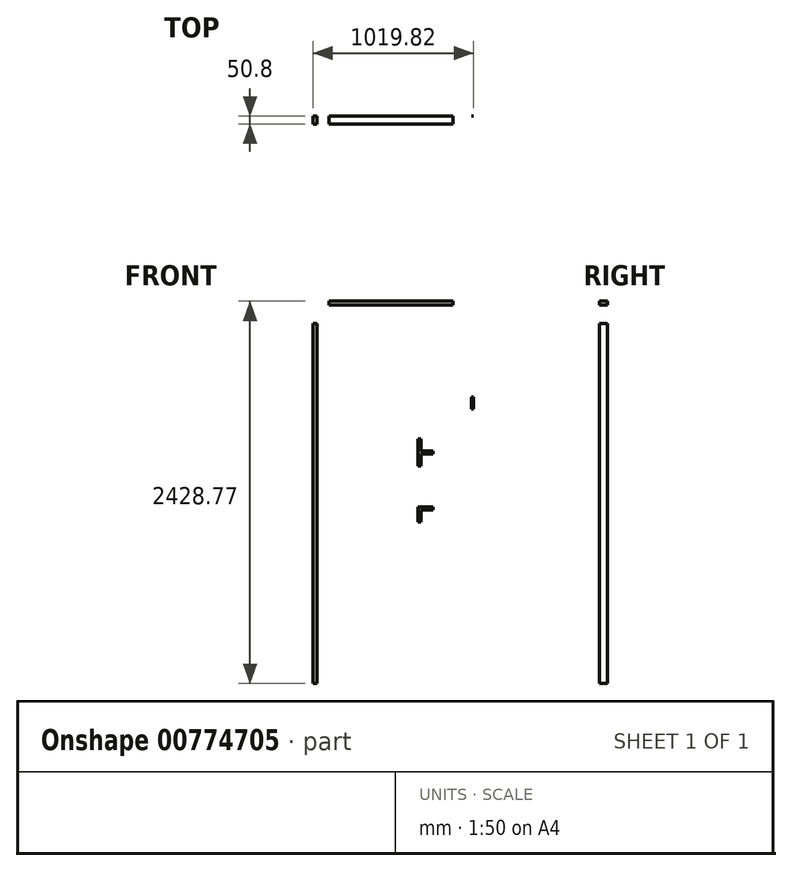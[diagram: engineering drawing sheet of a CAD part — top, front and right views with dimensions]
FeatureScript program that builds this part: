
annotation { "Feature Type Name" : "Feature", "Feature Type Description" : "" }
export const myFeature = defineFeature(function(context is Context, id is Id, definition is map)
    precondition{}
    {
        {
            var Q0;
            Q0=qCreatedBy(makeId("Front.planeOp"),FACE);
            var sketch = newSketch(context, id + "F0", { "sketchPlane" : qUnion([Q0])});
            skLineSegment(sketch, "E0.bottom", {"start": v(-40.5, 2159.15) * mm, "end": v(-15.1, 2159.15) * mm});
            skLineSegment(sketch, "E0.top", {"start": v(-40.5, -126.85) * mm, "end": v(-15.1, -126.85) * mm});
            skLineSegment(sketch, "E0.left", {"start": v(-40.5, 2159.15) * mm, "end": v(-40.5, -126.85) * mm});
            skLineSegment(sketch, "E0.right", {"start": v(-15.1, 2159.15) * mm, "end": v(-15.1, -126.85) * mm});
            skSolve(sketch);
        }
        {
            var Q0;
            Q0=qCreatedBy(makeId("Front.planeOp"),FACE);
            var sketch = newSketch(context, id + "F1", { "sketchPlane" : qUnion([Q0])});
            skLineSegment(sketch, "E1", {"start": v(61.76, 2301.92) * mm, "end": v(849.16, 2301.92) * mm});
            skLineSegment(sketch, "E2", {"start": v(849.16, 2301.92) * mm, "end": v(849.16, 2276.52) * mm});
            skLineSegment(sketch, "E3", {"start": v(849.16, 2276.52) * mm, "end": v(61.76, 2276.52) * mm});
            skLineSegment(sketch, "E4", {"start": v(61.76, 2276.52) * mm, "end": v(61.76, 2301.92) * mm});
            skSolve(sketch);
        }
        {
            var Q0;
            Q0=makeQuery(id+"F1.imprint","IMPRINT",FACE,{"disambiguationData":[TD([[makeQuery(id+"F1.imprint","IMPRINT",EDGE,{"derivedFrom":sQuery(id+"F1.wireOp",EDGE,"E1")}),-1.0]])]});
            extrude(context, id + "F2", {"entities" : qUnion([Q0]), "depth" : 50.8 * mm, "offsetDistance" : 25.4 * mm});
        }
        {
            var Q0;
            Q0 = qSketchRegion(id + "F0", true);
            extrude(context, id + "F3", {"entities" : qUnion([Q0]), "depth" : 50.8 * mm, "offsetDistance" : 25.4 * mm});
        }
        {
            var Q0;
            Q0=qCreatedBy(makeId("Front.planeOp"),FACE);
            var sketch = newSketch(context, id + "F4", { "sketchPlane" : qUnion([Q0])});
            skLineSegment(sketch, "E5", {"start": v(624.64, 898.32) * mm, "end": v(624.64, 993.57) * mm});
            skLineSegment(sketch, "E6", {"start": v(624.64, 993.57) * mm, "end": v(719.9, 993.57) * mm});
            skLineSegment(sketch, "E7", {"start": v(719.9, 993.57) * mm, "end": v(719.9, 974.52) * mm});
            skLineSegment(sketch, "E8", {"start": v(719.9, 974.52) * mm, "end": v(643.7, 974.52) * mm});
            skLineSegment(sketch, "E9", {"start": v(643.7, 974.52) * mm, "end": v(643.7, 898.32) * mm});
            skLineSegment(sketch, "E10", {"start": v(643.7, 898.32) * mm, "end": v(624.64, 898.32) * mm});
            skCircle(sketch, "E11", {"center": v(704.02, 984.05) * mm, "radius": 3.18 * mm});
            skPoint(sketch, "E11.centerSnap0", {"position": v(719.9, 984.05) * mm});
            skCircle(sketch, "E12", {"center": v(653.22, 984.05) * mm, "radius": 3.18 * mm});
            skCircle(sketch, "E13", {"center": v(634.17, 914.2) * mm, "radius": 3.18 * mm});
            skPoint(sketch, "E13.centerSnap0", {"position": v(634.17, 898.32) * mm});
            skCircle(sketch, "E14", {"center": v(634.17, 965) * mm, "radius": 3.18 * mm});
            skSolve(sketch);
        }
        {
            var Q0;
            Q0 = qSketchRegion(id + "F4", true);
            extrude(context, id + "F5", {"entities" : qUnion([Q0]), "depth" : 0.64 * mm, "offsetDistance" : 25.4 * mm});
        }
        {
            var Q0;
            Q0=qCreatedBy(makeId("Front.planeOp"),FACE);
            var sketch = newSketch(context, id + "F6", { "sketchPlane" : qUnion([Q0])});
            skLineSegment(sketch, "E15", {"start": v(625.48, 1254.4) * mm, "end": v(625.48, 1425.85) * mm});
            skLineSegment(sketch, "E16", {"start": v(625.48, 1425.85) * mm, "end": v(644.53, 1425.85) * mm});
            skLineSegment(sketch, "E17", {"start": v(644.53, 1425.85) * mm, "end": v(644.53, 1349.65) * mm});
            skLineSegment(sketch, "E18", {"start": v(644.53, 1349.65) * mm, "end": v(720.73, 1349.65) * mm});
            skLineSegment(sketch, "E19", {"start": v(720.73, 1349.65) * mm, "end": v(720.73, 1330.6) * mm});
            skLineSegment(sketch, "E20", {"start": v(720.73, 1330.6) * mm, "end": v(644.53, 1330.6) * mm});
            skLineSegment(sketch, "E21", {"start": v(644.53, 1330.6) * mm, "end": v(644.53, 1254.4) * mm});
            skLineSegment(sketch, "E22", {"start": v(644.53, 1254.4) * mm, "end": v(625.48, 1254.4) * mm});
            skCircle(sketch, "E23", {"center": v(704.86, 1340.13) * mm, "radius": 3.18 * mm});
            skPoint(sketch, "E23.centerSnap0", {"position": v(720.73, 1340.13) * mm});
            skCircle(sketch, "E24", {"center": v(654.06, 1340.13) * mm, "radius": 3.18 * mm});
            skCircle(sketch, "E25", {"center": v(635, 1409.98) * mm, "radius": 3.18 * mm});
            skPoint(sketch, "E25.centerSnap0", {"position": v(635, 1425.85) * mm});
            skCircle(sketch, "E26", {"center": v(635, 1359.18) * mm, "radius": 3.18 * mm});
            skCircle(sketch, "E27", {"center": v(635, 1270.28) * mm, "radius": 3.18 * mm});
            skPoint(sketch, "E27.centerSnap0", {"position": v(635, 1254.4) * mm});
            skCircle(sketch, "E28", {"center": v(635, 1321.08) * mm, "radius": 3.18 * mm});
            skSolve(sketch);
        }
        {
            var Q0;
            Q0 = qSketchRegion(id + "F6", true);
            extrude(context, id + "F7", {"entities" : qUnion([Q0]), "depth" : 0.64 * mm, "offsetDistance" : 25.4 * mm});
        }
        {
            var Q0;
            Q0=makeQuery(id+"F7.opExtrude","CAP_EDGE",EDGE,{"disambiguationData":[OSD([sQuery(id+"F6.wireOp",EDGE,"E23")])],"isStart":false});
            var Q1;
            Q1=makeQuery(id+"F7.opExtrude","CAP_EDGE",EDGE,{"disambiguationData":[OSD([sQuery(id+"F6.wireOp",EDGE,"E24")])],"isStart":false});
            var Q2;
            Q2=makeQuery(id+"F7.opExtrude","CAP_EDGE",EDGE,{"disambiguationData":[OSD([sQuery(id+"F6.wireOp",EDGE,"E28")])],"isStart":false});
            var Q3;
            Q3=makeQuery(id+"F7.opExtrude","CAP_EDGE",EDGE,{"disambiguationData":[OSD([sQuery(id+"F6.wireOp",EDGE,"E27")])],"isStart":false});
            var Q4;
            Q4=makeQuery(id+"F7.opExtrude","CAP_EDGE",EDGE,{"disambiguationData":[OSD([sQuery(id+"F6.wireOp",EDGE,"E26")])],"isStart":false});
            var Q5;
            Q5=makeQuery(id+"F7.opExtrude","CAP_EDGE",EDGE,{"disambiguationData":[OSD([sQuery(id+"F6.wireOp",EDGE,"E25")])],"isStart":false});
            chamfer(context, id + "F8", {"entities" : qUnion([Q0, Q1, Q2, Q3, Q4, Q5]), "width" : 0.64 * mm, "tangentPropagation" : true});
        }
        {
            var Q0;
            Q0=makeQuery(id+"F5.opExtrude","CAP_EDGE",EDGE,{"disambiguationData":[OSD([sQuery(id+"F4.wireOp",EDGE,"E11")])],"isStart":false});
            var Q1;
            Q1=makeQuery(id+"F5.opExtrude","CAP_EDGE",EDGE,{"disambiguationData":[OSD([sQuery(id+"F4.wireOp",EDGE,"E12")])],"isStart":false});
            var Q2;
            Q2=makeQuery(id+"F5.opExtrude","CAP_EDGE",EDGE,{"disambiguationData":[OSD([sQuery(id+"F4.wireOp",EDGE,"E14")])],"isStart":false});
            var Q3;
            Q3=makeQuery(id+"F5.opExtrude","CAP_EDGE",EDGE,{"disambiguationData":[OSD([sQuery(id+"F4.wireOp",EDGE,"E13")])],"isStart":false});
            chamfer(context, id + "F9", {"entities" : qUnion([Q0, Q1, Q2, Q3]), "width" : 0.64 * mm, "tangentPropagation" : true});
        }
        {
            var Q0;
            Q0=qCreatedBy(makeId("Front.planeOp"),FACE);
            var sketch = newSketch(context, id + "F10", { "sketchPlane" : qUnion([Q0])});
            skLineSegment(sketch, "E29", {"start": v(966.62, 1692.45) * mm, "end": v(979.32, 1692.45) * mm});
            skLineSegment(sketch, "E30", {"start": v(979.32, 1692.45) * mm, "end": v(979.32, 1616.25) * mm});
            skLineSegment(sketch, "E31", {"start": v(979.32, 1616.25) * mm, "end": v(966.62, 1616.25) * mm});
            skLineSegment(sketch, "E32", {"start": v(966.62, 1616.25) * mm, "end": v(966.62, 1692.45) * mm});
            skCircle(sketch, "E33", {"center": v(972.97, 1682.92) * mm, "radius": 3.18 * mm});
            skPoint(sketch, "E33.centerSnap0", {"position": v(972.97, 1692.45) * mm});
            skCircle(sketch, "E34", {"center": v(972.97, 1625.77) * mm, "radius": 3.18 * mm});
            skPoint(sketch, "E34.centerSnap0", {"position": v(972.97, 1616.25) * mm});
            skCircle(sketch, "E35", {"center": v(972.97, 1654.54) * mm, "radius": 3.18 * mm});
            skSolve(sketch);
        }
        {
            var Q0;
            Q0 = qSketchRegion(id + "F10", true);
            extrude(context, id + "F11", {"entities" : qUnion([Q0]), "depth" : 0.64 * mm, "offsetDistance" : 25.4 * mm});
        }
        {
            var Q0;
            Q0=makeQuery(id+"F11.opExtrude","CAP_EDGE",EDGE,{"disambiguationData":[OSD([sQuery(id+"F10.wireOp",EDGE,"E34")])],"isStart":false});
            var Q1;
            Q1=makeQuery(id+"F11.opExtrude","CAP_EDGE",EDGE,{"disambiguationData":[OSD([sQuery(id+"F10.wireOp",EDGE,"E35")])],"isStart":false});
            var Q2;
            Q2=makeQuery(id+"F11.opExtrude","CAP_EDGE",EDGE,{"disambiguationData":[OSD([sQuery(id+"F10.wireOp",EDGE,"E33")])],"isStart":false});
            chamfer(context, id + "F12", {"entities" : qUnion([Q0, Q1, Q2]), "width" : 0.64 * mm, "tangentPropagation" : true});
        }
    });
